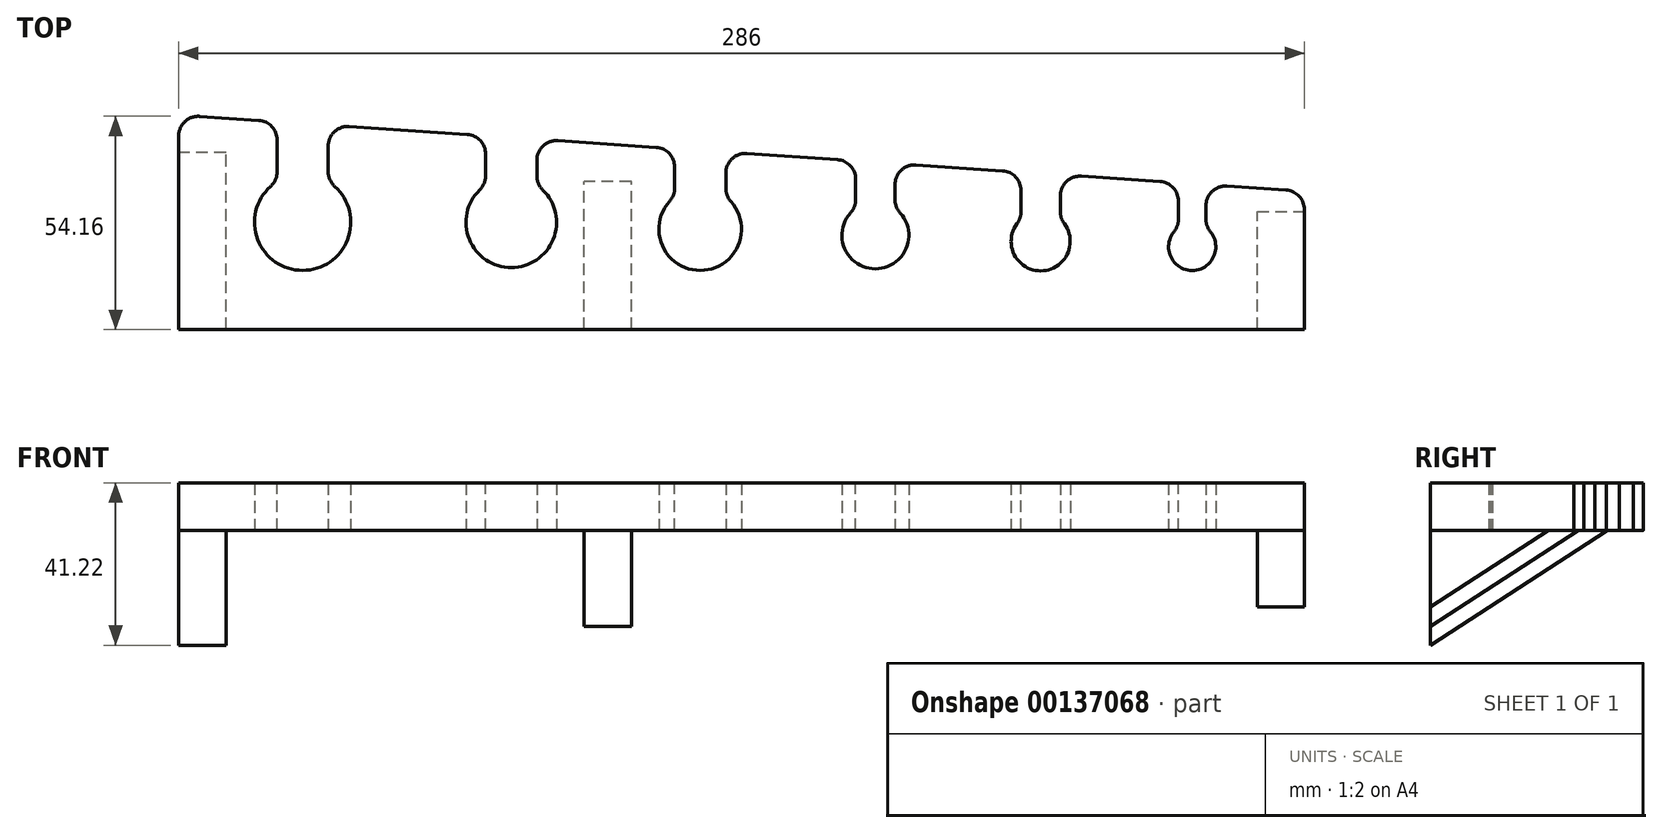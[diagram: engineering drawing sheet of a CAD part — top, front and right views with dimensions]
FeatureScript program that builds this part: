
annotation { "Feature Type Name" : "Feature", "Feature Type Description" : "" }
export const myFeature = defineFeature(function(context is Context, id is Id, definition is map)
    precondition{}
    {
        {
            var Q0;
            Q0=qCreatedBy(makeId("Top.planeOp"),FACE);
            var sketch = newSketch(context, id + "F0", { "sketchPlane" : qUnion([Q0])});
            skLineSegment(sketch, "E0.bottom", {"start": v(0, 0) * mm, "end": v(286, 0) * mm});
            skLineSegment(sketch, "E0.top", {"start": v(0, 54.51) * mm, "end": v(286, 35.1) * mm});
            skLineSegment(sketch, "E0.left", {"start": v(0, 0) * mm, "end": v(0, 54.51) * mm});
            skLineSegment(sketch, "E0.right", {"start": v(286, 0) * mm, "end": v(286, 35.1) * mm});
            skCircle(sketch, "E1", {"center": v(84.5, 27.23) * mm, "radius": 11.5 * mm});
            skCircle(sketch, "E2", {"center": v(132.5, 25.5) * mm, "radius": 10.5 * mm});
            skLineSegment(sketch, "E3", {"start": v(84.5, 27.23) * mm, "end": v(269.5, 20.57) * mm, "construction": true});
            skCircle(sketch, "E4", {"center": v(177, 23.9) * mm, "radius": 8.5 * mm});
            skCircle(sketch, "E5", {"center": v(219, 22.39) * mm, "radius": 7.5 * mm});
            skCircle(sketch, "E6", {"center": v(257.5, 21) * mm, "radius": 6 * mm});
            skLineSegment(sketch, "E7", {"start": v(194.14, 15) * mm, "end": v(50.72, 15) * mm, "construction": true});
            skLineSegment(sketch, "E8", {"start": v(73, 32.7) * mm, "end": v(73, 15.26) * mm, "construction": true});
            skLineSegment(sketch, "E9", {"start": v(103.38, 37.47) * mm, "end": v(248.59, 27.62) * mm, "construction": true});
            skLineSegment(sketch, "E10", {"start": v(84.5, 27.23) * mm, "end": v(84.5, 56.24) * mm});
            skLineSegment(sketch, "E11", {"start": v(132.5, 25.5) * mm, "end": v(132.5, 51.85) * mm});
            skLineSegment(sketch, "E12", {"start": v(177, 23.9) * mm, "end": v(177, 51.48) * mm});
            skLineSegment(sketch, "E13", {"start": v(219, 22.39) * mm, "end": v(219, 48.65) * mm});
            skLineSegment(sketch, "E14", {"start": v(257.5, 21) * mm, "end": v(257.5, 45.98) * mm});
            skArc(sketch, "E15.0.startCap", {"start": v(91, 27.23) * mm, "mid": v(84.5, 20.73) * mm, "end": v(78, 27.23) * mm});
            skArc(sketch, "E15.0.endCap", {"start": v(78, 56.24) * mm, "mid": v(84.5, 62.74) * mm, "end": v(91, 56.24) * mm});
            skLineSegment(sketch, "E15.0.left", {"start": v(78, 27.23) * mm, "end": v(78, 56.24) * mm});
            skLineSegment(sketch, "E15.0.right", {"start": v(91, 27.23) * mm, "end": v(91, 56.24) * mm});
            skArc(sketch, "E16.0.startCap", {"start": v(139, 25.5) * mm, "mid": v(132.5, 19) * mm, "end": v(126, 25.5) * mm});
            skArc(sketch, "E16.0.endCap", {"start": v(126, 51.85) * mm, "mid": v(132.5, 58.35) * mm, "end": v(139, 51.85) * mm});
            skLineSegment(sketch, "E16.0.left", {"start": v(126, 25.5) * mm, "end": v(126, 51.85) * mm});
            skLineSegment(sketch, "E16.0.right", {"start": v(139, 25.5) * mm, "end": v(139, 51.85) * mm});
            skArc(sketch, "E17.0.startCap", {"start": v(182, 23.9) * mm, "mid": v(177, 18.9) * mm, "end": v(172, 23.9) * mm});
            skArc(sketch, "E17.0.endCap", {"start": v(172, 51.48) * mm, "mid": v(177, 56.48) * mm, "end": v(182, 51.48) * mm});
            skLineSegment(sketch, "E17.0.left", {"start": v(172, 23.9) * mm, "end": v(172, 51.48) * mm});
            skLineSegment(sketch, "E17.0.right", {"start": v(182, 23.9) * mm, "end": v(182, 51.48) * mm});
            skArc(sketch, "E18.0.startCap", {"start": v(224, 22.39) * mm, "mid": v(219, 17.39) * mm, "end": v(214, 22.39) * mm});
            skArc(sketch, "E18.0.endCap", {"start": v(214, 48.65) * mm, "mid": v(219, 53.65) * mm, "end": v(224, 48.65) * mm});
            skLineSegment(sketch, "E18.0.left", {"start": v(214, 22.39) * mm, "end": v(214, 48.65) * mm});
            skLineSegment(sketch, "E18.0.right", {"start": v(224, 22.39) * mm, "end": v(224, 48.65) * mm});
            skArc(sketch, "E19.0.startCap", {"start": v(261, 21) * mm, "mid": v(257.5, 17.5) * mm, "end": v(254, 21) * mm});
            skArc(sketch, "E19.0.endCap", {"start": v(254, 45.98) * mm, "mid": v(257.5, 49.48) * mm, "end": v(261, 45.98) * mm});
            skLineSegment(sketch, "E19.0.left", {"start": v(254, 21) * mm, "end": v(254, 45.98) * mm});
            skLineSegment(sketch, "E19.0.right", {"start": v(261, 21) * mm, "end": v(261, 45.98) * mm});
            skCircle(sketch, "E20", {"center": v(31.5, 27.23) * mm, "radius": 12.23 * mm});
            skLineSegment(sketch, "E21", {"start": v(31.5, 27.23) * mm, "end": v(84.5, 27.23) * mm, "construction": true});
            skLineSegment(sketch, "E22", {"start": v(31.5, 27.23) * mm, "end": v(31.5, 66.48) * mm, "construction": true});
            skArc(sketch, "E23.0.startCap", {"start": v(38, 27.23) * mm, "mid": v(31.5, 20.73) * mm, "end": v(25, 27.23) * mm});
            skArc(sketch, "E23.0.endCap", {"start": v(25, 66.48) * mm, "mid": v(31.5, 72.98) * mm, "end": v(38, 66.48) * mm});
            skLineSegment(sketch, "E23.0.left", {"start": v(25, 27.23) * mm, "end": v(25, 66.48) * mm});
            skLineSegment(sketch, "E23.0.right", {"start": v(38, 27.23) * mm, "end": v(38, 66.48) * mm});
            skCircle(sketch, "E24", {"center": v(31.5, 27.23) * mm, "radius": 22 * mm, "construction": true});
            skCircle(sketch, "E25", {"center": v(84.5, 27.23) * mm, "radius": 18 * mm, "construction": true});
            skCircle(sketch, "E26", {"center": v(132.5, 25.5) * mm, "radius": 16.5 * mm, "construction": true});
            skCircle(sketch, "E27", {"center": v(177, 23.9) * mm, "radius": 15 * mm, "construction": true});
            skCircle(sketch, "E28", {"center": v(219, 22.39) * mm, "radius": 14 * mm, "construction": true});
            skCircle(sketch, "E29", {"center": v(257.5, 21) * mm, "radius": 12 * mm, "construction": true});
            skSolve(sketch);
        }
        {
            var Q0;
            Q0=makeQuery(id+"F0.imprint","IMPRINT",FACE,{"disambiguationData":[TD([[makeQuery(id+"F0.imprint","IMPRINT",EDGE,{"derivedFrom":sQuery(id+"F0.wireOp",EDGE,"E0.bottom")}),1.0]])]});
            extrude(context, id + "F1", {"entities" : qUnion([Q0]), "depth" : 12 * mm});
        }
        {
            var Q0;
            Q0=makeQuery(id+"F1.opExtrude","SWEPT_EDGE",EDGE,{"disambiguationData":[OSD([sQuery(id+"F0.wireOp",EDGE,"E0.top"),sQuery(id+"F0.wireOp",EDGE,"E0.right")])]});
            var Q1;
            Q1=makeQuery(id+"F1.opExtrude","SWEPT_EDGE",EDGE,{"disambiguationData":[OSD([sQuery(id+"F0.wireOp",EDGE,"E0.top"),sQuery(id+"F0.wireOp",EDGE,"E19.0.right")])]});
            var Q2;
            Q2=makeQuery(id+"F1.opExtrude","SWEPT_EDGE",EDGE,{"disambiguationData":[OSD([sQuery(id+"F0.wireOp",EDGE,"E0.top"),sQuery(id+"F0.wireOp",EDGE,"E19.0.left")])]});
            var Q3;
            Q3=makeQuery(id+"F1.opExtrude","SWEPT_EDGE",EDGE,{"disambiguationData":[OSD([sQuery(id+"F0.wireOp",EDGE,"E0.top"),sQuery(id+"F0.wireOp",EDGE,"E18.0.right")])]});
            var Q4;
            Q4=makeQuery(id+"F1.opExtrude","SWEPT_EDGE",EDGE,{"disambiguationData":[OSD([sQuery(id+"F0.wireOp",EDGE,"E0.top"),sQuery(id+"F0.wireOp",EDGE,"E18.0.left")])]});
            var Q5;
            Q5=makeQuery(id+"F1.opExtrude","SWEPT_EDGE",EDGE,{"disambiguationData":[OSD([sQuery(id+"F0.wireOp",EDGE,"E0.top"),sQuery(id+"F0.wireOp",EDGE,"E17.0.right")])]});
            var Q6;
            Q6=makeQuery(id+"F1.opExtrude","SWEPT_EDGE",EDGE,{"disambiguationData":[OSD([sQuery(id+"F0.wireOp",EDGE,"E0.top"),sQuery(id+"F0.wireOp",EDGE,"E17.0.left")])]});
            var Q7;
            Q7=makeQuery(id+"F1.opExtrude","SWEPT_EDGE",EDGE,{"disambiguationData":[OSD([sQuery(id+"F0.wireOp",EDGE,"E0.top"),sQuery(id+"F0.wireOp",EDGE,"E16.0.right")])]});
            var Q8;
            Q8=makeQuery(id+"F1.opExtrude","SWEPT_EDGE",EDGE,{"disambiguationData":[OSD([sQuery(id+"F0.wireOp",EDGE,"E0.top"),sQuery(id+"F0.wireOp",EDGE,"E16.0.left")])]});
            var Q9;
            Q9=makeQuery(id+"F1.opExtrude","SWEPT_EDGE",EDGE,{"disambiguationData":[OSD([sQuery(id+"F0.wireOp",EDGE,"E0.top"),sQuery(id+"F0.wireOp",EDGE,"E15.0.right")])]});
            var Q10;
            Q10=makeQuery(id+"F1.opExtrude","SWEPT_EDGE",EDGE,{"disambiguationData":[OSD([sQuery(id+"F0.wireOp",EDGE,"E0.top"),sQuery(id+"F0.wireOp",EDGE,"E15.0.left")])]});
            var Q11;
            Q11=makeQuery(id+"F1.opExtrude","SWEPT_EDGE",EDGE,{"disambiguationData":[OSD([sQuery(id+"F0.wireOp",EDGE,"E0.top"),sQuery(id+"F0.wireOp",EDGE,"E23.0.right")])]});
            var Q12;
            Q12=makeQuery(id+"F1.opExtrude","SWEPT_EDGE",EDGE,{"disambiguationData":[OSD([sQuery(id+"F0.wireOp",EDGE,"E0.top"),sQuery(id+"F0.wireOp",EDGE,"E23.0.left")])]});
            var Q13;
            Q13=makeQuery(id+"F1.opExtrude","SWEPT_EDGE",EDGE,{"disambiguationData":[OSD([sQuery(id+"F0.wireOp",EDGE,"E0.top"),sQuery(id+"F0.wireOp",EDGE,"E0.left")])]});
            var Q14;
            Q14=makeQuery(id+"F1.opExtrude","SWEPT_EDGE",EDGE,{"disambiguationData":[OSD([sQuery(id+"F0.wireOp",EDGE,"E20"),sQuery(id+"F0.wireOp",EDGE,"E23.0.left")])]});
            var Q15;
            Q15=makeQuery(id+"F1.opExtrude","SWEPT_EDGE",EDGE,{"disambiguationData":[OSD([sQuery(id+"F0.wireOp",EDGE,"E20"),sQuery(id+"F0.wireOp",EDGE,"E23.0.right")])]});
            var Q16;
            Q16=makeQuery(id+"F1.opExtrude","SWEPT_EDGE",EDGE,{"disambiguationData":[OSD([sQuery(id+"F0.wireOp",EDGE,"E1"),sQuery(id+"F0.wireOp",EDGE,"E15.0.right")])]});
            var Q17;
            Q17=makeQuery(id+"F1.opExtrude","SWEPT_EDGE",EDGE,{"disambiguationData":[OSD([sQuery(id+"F0.wireOp",EDGE,"E2"),sQuery(id+"F0.wireOp",EDGE,"E16.0.right")])]});
            var Q18;
            Q18=makeQuery(id+"F1.opExtrude","SWEPT_EDGE",EDGE,{"disambiguationData":[OSD([sQuery(id+"F0.wireOp",EDGE,"E4"),sQuery(id+"F0.wireOp",EDGE,"E17.0.right")])]});
            var Q19;
            Q19=makeQuery(id+"F1.opExtrude","SWEPT_EDGE",EDGE,{"disambiguationData":[OSD([sQuery(id+"F0.wireOp",EDGE,"E1"),sQuery(id+"F0.wireOp",EDGE,"E15.0.left")])]});
            var Q20;
            Q20=makeQuery(id+"F1.opExtrude","SWEPT_EDGE",EDGE,{"disambiguationData":[OSD([sQuery(id+"F0.wireOp",EDGE,"E2"),sQuery(id+"F0.wireOp",EDGE,"E16.0.left")])]});
            var Q21;
            Q21=makeQuery(id+"F1.opExtrude","SWEPT_EDGE",EDGE,{"disambiguationData":[OSD([sQuery(id+"F0.wireOp",EDGE,"E5"),sQuery(id+"F0.wireOp",EDGE,"E18.0.left")])]});
            var Q22;
            Q22=makeQuery(id+"F1.opExtrude","SWEPT_EDGE",EDGE,{"disambiguationData":[OSD([sQuery(id+"F0.wireOp",EDGE,"E6"),sQuery(id+"F0.wireOp",EDGE,"E19.0.left")])]});
            var Q23;
            Q23=makeQuery(id+"F1.opExtrude","SWEPT_EDGE",EDGE,{"disambiguationData":[OSD([sQuery(id+"F0.wireOp",EDGE,"E6"),sQuery(id+"F0.wireOp",EDGE,"E19.0.right")])]});
            var Q24;
            Q24=makeQuery(id+"F1.opExtrude","SWEPT_EDGE",EDGE,{"disambiguationData":[OSD([sQuery(id+"F0.wireOp",EDGE,"E5"),sQuery(id+"F0.wireOp",EDGE,"E18.0.right")])]});
            var Q25;
            Q25=makeQuery(id+"F1.opExtrude","SWEPT_EDGE",EDGE,{"disambiguationData":[OSD([sQuery(id+"F0.wireOp",EDGE,"E4"),sQuery(id+"F0.wireOp",EDGE,"E17.0.left")])]});
            fillet(context, id + "F2", {"entities" : qUnion([Q0, Q1, Q2, Q3, Q4, Q5, Q6, Q7, Q8, Q9, Q10, Q11, Q12, Q13, Q14, Q15, Q16, Q17, Q18, Q19, Q20, Q21, Q22, Q23, Q24, Q25]), "radius" : 5 * mm, "tangentPropagation" : true, "allowEdgeOverflow" : false});
        }
        {
            var Q0;
            Q0=qCreatedBy(makeId("Right.planeOp"),FACE);
            var sketch = newSketch(context, id + "F3", { "sketchPlane" : qUnion([Q0])});
            skLineSegment(sketch, "E30", {"start": v(0, 0) * mm, "end": v(45, 0) * mm});
            skLineSegment(sketch, "E31", {"start": v(45, 0) * mm, "end": v(0, -29.22) * mm});
            skLineSegment(sketch, "E32", {"start": v(0, -29.22) * mm, "end": v(0, 0) * mm});
            skSolve(sketch);
        }
        {
            var Q0;
            Q0 = qSketchRegion(id + "F3", true);
            extrude(context, id + "F4", {"entities" : qUnion([Q0]), "depth" : 12 * mm});
        }
        {
            var Q0;
            Q0=makeQuery(id+"F1.opExtrude","SWEPT_FACE",FACE,{"disambiguationData":[OSD([sQuery(id+"F0.wireOp",EDGE,"E0.right")])]});
            var sketch = newSketch(context, id + "F5", { "sketchPlane" : qUnion([Q0])});
            skLineSegment(sketch, "E33", {"start": v(0, 0) * mm, "end": v(0, -19.48) * mm});
            skLineSegment(sketch, "E34", {"start": v(0, -19.48) * mm, "end": v(30, 0) * mm});
            skLineSegment(sketch, "E35", {"start": v(30, 0) * mm, "end": v(0, 0) * mm});
            skSolve(sketch);
        }
        {
            var Q0;
            Q0 = qSketchRegion(id + "F5", true);
            extrude(context, id + "F6", {"entities" : qUnion([Q0]), "oppositeDirection" : true, "depth" : 12 * mm});
        }
        {
            var Q0;
            Q0=qCreatedBy(makeId("Right.planeOp"),FACE);
            cPlane(context, id + "F7", {"entities" : qUnion([Q0]), "cplaneType" : CPlaneType.OFFSET, "offset" : 103 * mm, "width" : 150 * mm, "height" : 150 * mm});
        }
        {
            var Q0;
            Q0=qCreatedBy(id+"F7.planeOp",FACE);
            var sketch = newSketch(context, id + "F8", { "sketchPlane" : qUnion([Q0])});
            skLineSegment(sketch, "E36", {"start": v(37.62, 0) * mm, "end": v(0, 0) * mm});
            skLineSegment(sketch, "E37", {"start": v(0, 0) * mm, "end": v(0, -24.43) * mm});
            skLineSegment(sketch, "E38", {"start": v(0, -24.43) * mm, "end": v(37.62, 0) * mm});
            skSolve(sketch);
        }
        {
            var Q0;
            Q0 = qSketchRegion(id + "F8", true);
            extrude(context, id + "F9", {"entities" : qUnion([Q0]), "depth" : 12 * mm});
        }
    });
